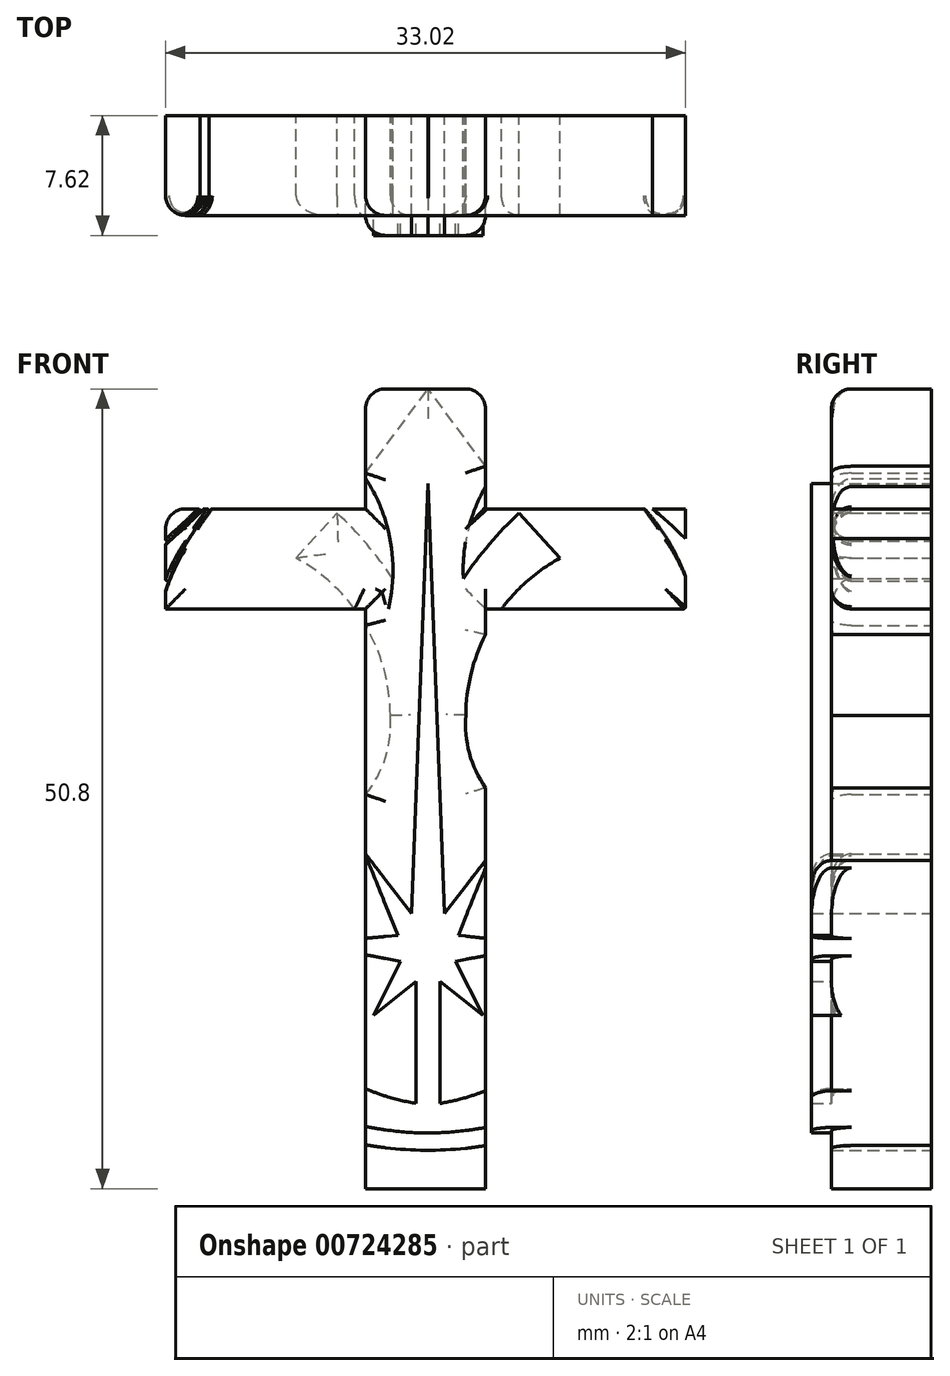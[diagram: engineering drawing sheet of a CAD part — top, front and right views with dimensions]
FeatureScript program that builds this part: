
annotation { "Feature Type Name" : "Feature", "Feature Type Description" : "" }
export const myFeature = defineFeature(function(context is Context, id is Id, definition is map)
    precondition{}
    {
        {
            var Q0;
            Q0=qCreatedBy(makeId("Front.planeOp"),FACE);
            var sketch = newSketch(context, id + "F0", { "sketchPlane" : qUnion([Q0])});
            skLineSegment(sketch, "E0", {"start": v(0, 50.8) * mm, "end": v(-7.62, 50.8) * mm});
            skLineSegment(sketch, "E1", {"start": v(-7.62, 0) * mm, "end": v(0, 0) * mm});
            skLineSegment(sketch, "E2", {"start": v(-7.62, 43.18) * mm, "end": v(-20.32, 43.18) * mm});
            skLineSegment(sketch, "E3", {"start": v(-20.32, 43.18) * mm, "end": v(-20.32, 36.83) * mm});
            skLineSegment(sketch, "E4", {"start": v(12.7, 36.83) * mm, "end": v(12.7, 43.18) * mm});
            skLineSegment(sketch, "E5", {"start": v(12.7, 43.18) * mm, "end": v(0, 43.18) * mm});
            skLineSegment(sketch, "E6", {"start": v(-20.32, 36.83) * mm, "end": v(-7.62, 36.83) * mm});
            skLineSegment(sketch, "E7", {"start": v(12.7, 36.83) * mm, "end": v(0, 36.83) * mm});
            skLineSegment(sketch, "E8", {"start": v(-7.62, 0) * mm, "end": v(-7.62, 36.83) * mm});
            skLineSegment(sketch, "E9", {"start": v(0, 36.83) * mm, "end": v(0, 0) * mm});
            skLineSegment(sketch, "E10", {"start": v(0, 43.18) * mm, "end": v(0, 50.8) * mm});
            skLineSegment(sketch, "E11", {"start": v(-7.62, 43.18) * mm, "end": v(-7.62, 50.8) * mm});
            skSolve(sketch);
        }
        {
            var Q0;
            Q0=qCreatedBy(makeId("Front.planeOp"),FACE);
            var sketch = newSketch(context, id + "F1", { "sketchPlane" : qUnion([Q0])});
            skArc(sketch, "E12", {"start": v(-17.9, 43.18) * mm, "mid": v(-19.15, 42.1) * mm, "end": v(-20.32, 40.94) * mm});
            skArc(sketch, "E13", {"start": v(-7.62, 3.95) * mm, "mid": v(-5.64, 3.65) * mm, "end": v(-3.65, 3.53) * mm});
            skArc(sketch, "E14", {"start": v(-7.62, 6.35) * mm, "mid": v(-6.04, 5.78) * mm, "end": v(-4.4, 5.41) * mm});
            skArc(sketch, "E15", {"start": v(-5.9, 38.75) * mm, "mid": v(-6.25, 42.07) * mm, "end": v(-7.62, 45.11) * mm});
            skArc(sketch, "E16", {"start": v(-5.9, 38.75) * mm, "mid": v(-7.54, 40.93) * mm, "end": v(-9.43, 42.9) * mm});
            skArc(sketch, "E17", {"start": v(-17.4, 43.18) * mm, "mid": v(-19.16, 40.71) * mm, "end": v(-20.32, 37.92) * mm});
            skArc(sketch, "E18", {"start": v(-7.62, 25.04) * mm, "mid": v(-6.35, 27.4) * mm, "end": v(-6.05, 30.07) * mm});
            skArc(sketch, "E19", {"start": v(-6.05, 30.07) * mm, "mid": v(-6.46, 33.03) * mm, "end": v(-7.62, 35.78) * mm});
            skLineSegment(sketch, "E20", {"start": v(-12.04, 40.06) * mm, "end": v(-9.43, 42.9) * mm});
            skLineSegment(sketch, "E21", {"start": v(-7.62, 45.45) * mm, "end": v(-3.65, 50.82) * mm});
            skLineSegment(sketch, "E22", {"start": v(-4.4, 5.41) * mm, "end": v(-4.4, 13.16) * mm});
            skLineSegment(sketch, "E23", {"start": v(-4.4, 13.16) * mm, "end": v(-7.12, 11) * mm});
            skLineSegment(sketch, "E24", {"start": v(-7.12, 11) * mm, "end": v(-5.4, 14.45) * mm});
            skLineSegment(sketch, "E25", {"start": v(-5.4, 14.45) * mm, "end": v(-7.62, 14.86) * mm});
            skLineSegment(sketch, "E26", {"start": v(-5.57, 16.1) * mm, "end": v(-7.62, 21.17) * mm});
            skLineSegment(sketch, "E27", {"start": v(-7.62, 21.26) * mm, "end": v(-4.7, 17.49) * mm});
            skLineSegment(sketch, "E28", {"start": v(-4.7, 17.49) * mm, "end": v(-3.65, 44.78) * mm});
            skLineSegment(sketch, "E29.MirrorCS", {"start": v(0, 45.88) * mm, "end": v(-3.65, 50.82) * mm});
            skArc(sketch, "E30.MirrorCS", {"start": v(-1.4, 38.75) * mm, "mid": v(0.24, 40.93) * mm, "end": v(2.13, 42.9) * mm});
            skLineSegment(sketch, "E31.MirrorCS", {"start": v(4.74, 40.06) * mm, "end": v(2.13, 42.9) * mm});
            skArc(sketch, "E32.MirrorCS", {"start": v(-1.25, 30.07) * mm, "mid": v(-0.92, 32.7) * mm, "end": v(0, 35.19) * mm});
            skArc(sketch, "E33.MirrorCS", {"start": v(0, 25.47) * mm, "mid": v(-1.02, 27.66) * mm, "end": v(-1.25, 30.07) * mm});
            skArc(sketch, "E34.MirrorCS", {"start": v(10.11, 43.18) * mm, "mid": v(11.6, 41.16) * mm, "end": v(12.7, 38.9) * mm});
            skArc(sketch, "E35.MirrorCS", {"start": v(0, 3.89) * mm, "mid": v(-1.82, 3.63) * mm, "end": v(-3.65, 3.53) * mm});
            skLineSegment(sketch, "E36.MirrorCS", {"start": v(-2.9, 5.41) * mm, "end": v(-2.9, 13.16) * mm});
            skLineSegment(sketch, "E37.MirrorCS", {"start": v(-2.9, 13.16) * mm, "end": v(-0.18, 11) * mm});
            skLineSegment(sketch, "E38.MirrorCS", {"start": v(-0.18, 11) * mm, "end": v(-1.9, 14.45) * mm});
            skLineSegment(sketch, "E39.MirrorCS", {"start": v(-1.9, 14.45) * mm, "end": v(0, 14.8) * mm});
            skLineSegment(sketch, "E40.MirrorCS", {"start": v(0, 15.9) * mm, "end": v(-1.73, 16.1) * mm});
            skLineSegment(sketch, "E41.MirrorCS", {"start": v(-1.73, 16.1) * mm, "end": v(0, 20.37) * mm});
            skLineSegment(sketch, "E42.MirrorCS", {"start": v(0, 20.85) * mm, "end": v(-2.6, 17.49) * mm});
            skLineSegment(sketch, "E43.MirrorCS", {"start": v(-2.6, 17.49) * mm, "end": v(-3.65, 44.78) * mm});
            skArc(sketch, "E44.MirrorCS", {"start": v(-1.4, 38.75) * mm, "mid": v(-1.12, 41.77) * mm, "end": v(0, 44.59) * mm});
            skArc(sketch, "E45.MirrorCS", {"start": v(0, 6.22) * mm, "mid": v(-1.43, 5.74) * mm, "end": v(-2.9, 5.41) * mm});
            skLineSegment(sketch, "E46.0.0", {"start": v(0, 0) * mm, "end": v(0, 36.83) * mm});
            skLineSegment(sketch, "E46.0.1", {"start": v(0, 36.83) * mm, "end": v(12.7, 36.83) * mm});
            skLineSegment(sketch, "E46.0.2", {"start": v(12.7, 36.83) * mm, "end": v(12.7, 43.18) * mm});
            skLineSegment(sketch, "E46.0.3", {"start": v(12.7, 43.18) * mm, "end": v(0, 43.18) * mm});
            skLineSegment(sketch, "E46.0.4", {"start": v(0, 43.18) * mm, "end": v(0, 50.8) * mm});
            skLineSegment(sketch, "E46.0.5", {"start": v(0, 50.8) * mm, "end": v(-7.62, 50.8) * mm});
            skLineSegment(sketch, "E46.0.6", {"start": v(-7.62, 50.8) * mm, "end": v(-7.62, 43.18) * mm});
            skLineSegment(sketch, "E46.0.7", {"start": v(-7.62, 43.18) * mm, "end": v(-20.32, 43.18) * mm});
            skLineSegment(sketch, "E46.0.8", {"start": v(-20.32, 43.18) * mm, "end": v(-20.32, 36.83) * mm});
            skLineSegment(sketch, "E46.0.9", {"start": v(-20.32, 36.83) * mm, "end": v(-7.62, 36.83) * mm});
            skLineSegment(sketch, "E46.0.10", {"start": v(-7.62, 36.83) * mm, "end": v(-7.62, 0) * mm});
            skLineSegment(sketch, "E46.0.11", {"start": v(-7.62, 0) * mm, "end": v(0, 0) * mm});
            skArc(sketch, "E47.trimOffspring", {"start": v(-7.62, 2.79) * mm, "mid": v(-3.81, 2.44) * mm, "end": v(0, 2.73) * mm});
            skArc(sketch, "E48.trimOffspring", {"start": v(12.7, 41.28) * mm, "mid": v(11.68, 42.26) * mm, "end": v(10.6, 43.18) * mm});
            skPoint(sketch, "E49.end.orphan", {"position": v(-18.43, 15.28) * mm});
            skPoint(sketch, "E50.end.orphan", {"position": v(-18.43, 11.36) * mm});
            skLineSegment(sketch, "E51", {"start": v(-5.57, 16.1) * mm, "end": v(-7.62, 15.9) * mm});
            skArc(sketch, "E52.trimOffspring", {"start": v(1.02, 36.83) * mm, "mid": v(2.7, 38.65) * mm, "end": v(4.74, 40.06) * mm});
            skArc(sketch, "E53.trimOffspring", {"start": v(-8.32, 36.83) * mm, "mid": v(-10, 38.65) * mm, "end": v(-12.04, 40.06) * mm});
            skSolve(sketch);
        }
        {
            var Q0;
            {var subQ4=sQuery(id+"F1.wireOp",EDGE,"E13");Q0=makeQuery(id+"F1.imprint","IMPRINT",FACE,{"disambiguationData":[TD([[makeQuery(id+"F1.imprint","IMPRINT",EDGE,{"derivedFrom":subQ4}),1.0]])]});}
            extrude(context, id + "F2", {"entities" : qUnion([Q0]), "depth" : 7.62 * mm, "offsetDistance" : 25.4 * mm});
        }
        {
            var Q0;
            {var subQ0=sQuery(id+"F1.wireOp",EDGE,"E12");Q0=makeQuery(id+"F1.imprint","IMPRINT",FACE,{"disambiguationData":[TD([[makeQuery(id+"F1.imprint","IMPRINT",EDGE,{"derivedFrom":subQ0}),1.0]])]});}
            var Q1;
            {var subQ0=sQuery(id+"F1.wireOp",EDGE,"E34.MirrorCS");Q1=makeQuery(id+"F1.imprint","IMPRINT",FACE,{"disambiguationData":[TD([[makeQuery(id+"F1.imprint","IMPRINT",EDGE,{"derivedFrom":subQ0}),1.0]])]});}
            var Q2;
            {var subQ1=sQuery(id+"F1.wireOp",EDGE,"E15");Q2=makeQuery(id+"F1.imprint","IMPRINT",FACE,{"disambiguationData":[TD([[makeQuery(id+"F1.imprint","IMPRINT",EDGE,{"derivedFrom":subQ1}),-1.0]])]});}
            var Q3;
            Q3=makeQuery(id+"F1.imprint","IMPRINT",FACE,{"disambiguationData":[TD([[makeQuery(id+"F1.imprint","IMPRINT",EDGE,{"derivedFrom":sQuery(id+"F1.wireOp",EDGE,"E36.MirrorCS")}),-1.0]])]});
            var Q4;
            {var subQ0=sQuery(id+"F1.wireOp",EDGE,"E40.MirrorCS");Q4=makeQuery(id+"F1.imprint","IMPRINT",FACE,{"disambiguationData":[TD([[makeQuery(id+"F1.imprint","IMPRINT",EDGE,{"derivedFrom":subQ0}),-1.0]])]});}
            var Q5;
            {var subQ0=sQuery(id+"F1.wireOp",EDGE,"E26");Q5=makeQuery(id+"F1.imprint","IMPRINT",FACE,{"disambiguationData":[TD([[makeQuery(id+"F1.imprint","IMPRINT",EDGE,{"derivedFrom":subQ0}),1.0]])]});}
            var Q6;
            {var subQ0=sQuery(id+"F1.wireOp",EDGE,"E14");Q6=makeQuery(id+"F1.imprint","IMPRINT",FACE,{"disambiguationData":[TD([[makeQuery(id+"F1.imprint","IMPRINT",EDGE,{"derivedFrom":subQ0}),1.0]])]});}
            var Q7;
            {var subQ1=sQuery(id+"F1.wireOp",EDGE,"E13");Q7=makeQuery(id+"F1.imprint","IMPRINT",FACE,{"disambiguationData":[TD([[makeQuery(id+"F1.imprint","IMPRINT",EDGE,{"derivedFrom":subQ1}),-1.0]])]});}
            extrude(context, id + "F3", {"entities" : qUnion([Q0, Q1, Q2, Q3, Q4, Q5, Q6, Q7]), "operationType" : NewBodyOperationType.ADD, "depth" : 6.35 * mm, "offsetDistance" : 25.4 * mm});
        }
        {
            var Q0;
            {var subQ3=sQuery(id+"F1.wireOp",EDGE,"E48.trimOffspring");Q0=makeQuery(id+"F1.imprint","IMPRINT",FACE,{"disambiguationData":[TD([[makeQuery(id+"F1.imprint","IMPRINT",EDGE,{"derivedFrom":subQ3}),-1.0]])]});}
            var Q1;
            Q1=makeQuery(id+"F1.imprint","IMPRINT",FACE,{"disambiguationData":[TD([[makeQuery(id+"F1.imprint","IMPRINT",EDGE,{"derivedFrom":sQuery(id+"F1.wireOp",EDGE,"E30.MirrorCS")}),1.0]])]});
            var Q2;
            {var subQ0=sQuery(id+"F1.wireOp",EDGE,"E46.0.4");var subQ1=sQuery(id+"F1.wireOp",EDGE,"E29.MirrorCS");var subQ2=makeQuery(id+"F1.imprint","INTERSECT",VERTEX,{"derivedFrom":[subQ1,subQ0]});Q2=makeQuery(id+"F1.imprint","IMPRINT",FACE,{"disambiguationData":[TD([[makeQuery(id+"F1.imprint","IMPRINT",EDGE,{"disambiguationData":[TD([[subQ2,-1.0]])],"derivedFrom":subQ1}),-1.0]])]});}
            var Q3;
            {var subQ0=sQuery(id+"F1.wireOp",EDGE,"E46.0.6");var subQ1=sQuery(id+"F1.wireOp",EDGE,"E21");var subQ2=makeQuery(id+"F1.imprint","INTERSECT",VERTEX,{"derivedFrom":[subQ1,subQ0]});Q3=makeQuery(id+"F1.imprint","IMPRINT",FACE,{"disambiguationData":[TD([[makeQuery(id+"F1.imprint","IMPRINT",EDGE,{"disambiguationData":[TD([[subQ2,-1.0]])],"derivedFrom":subQ1}),1.0]])]});}
            var Q4;
            {var subQ4=sQuery(id+"F1.wireOp",EDGE,"E15");Q4=makeQuery(id+"F1.imprint","IMPRINT",FACE,{"disambiguationData":[TD([[makeQuery(id+"F1.imprint","IMPRINT",EDGE,{"derivedFrom":subQ4}),1.0]])]});}
            var Q5;
            {var subQ0=sQuery(id+"F1.wireOp",EDGE,"E12");Q5=makeQuery(id+"F1.imprint","IMPRINT",FACE,{"disambiguationData":[TD([[makeQuery(id+"F1.imprint","IMPRINT",EDGE,{"derivedFrom":subQ0}),-1.0]])]});}
            var Q6;
            {var subQ0=sQuery(id+"F1.wireOp",EDGE,"E32.MirrorCS");Q6=makeQuery(id+"F1.imprint","IMPRINT",FACE,{"disambiguationData":[TD([[makeQuery(id+"F1.imprint","IMPRINT",EDGE,{"derivedFrom":subQ0}),-1.0]])]});}
            var Q7;
            {var subQ0=sQuery(id+"F1.wireOp",EDGE,"E18");Q7=makeQuery(id+"F1.imprint","IMPRINT",FACE,{"disambiguationData":[TD([[makeQuery(id+"F1.imprint","IMPRINT",EDGE,{"derivedFrom":subQ0}),1.0]])]});}
            var Q8;
            {var subQ0=sQuery(id+"F1.wireOp",EDGE,"E46.0.11");Q8=makeQuery(id+"F1.imprint","IMPRINT",FACE,{"disambiguationData":[TD([[makeQuery(id+"F1.imprint","IMPRINT",EDGE,{"derivedFrom":subQ0}),1.0]])]});}
            extrude(context, id + "F4", {"entities" : qUnion([Q0, Q1, Q2, Q3, Q4, Q5, Q6, Q7, Q8]), "depth" : 6.35 * mm, "offsetDistance" : 25.4 * mm});
        }
        {
            var Q0;
            {var subQ0=sQuery(id+"F1.wireOp",EDGE,"E46.0.7");Q0=makeQuery(id+"F4.opExtrude","CAP_EDGE",EDGE,{"disambiguationData":[OSD([subQ0]),TDD([makeQuery(id+"F1.imprint","IMPRINT",EDGE,{"disambiguationData":[TD([[makeQuery(id+"F1.imprint","INTERSECT",VERTEX,{"derivedFrom":[sQuery(id+"F1.wireOp",EDGE,"E17"),subQ0]}),1.0]])],"derivedFrom":subQ0})])],"isStart":false});}
            var Q1;
            Q1=makeQuery(id+"F3.opExtrude","CAP_EDGE",EDGE,{"disambiguationData":[OSD([sQuery(id+"F1.wireOp",EDGE,"E46.0.7")])],"isStart":false});
            var Q2;
            {var subQ0=sQuery(id+"F1.wireOp",EDGE,"E46.0.7");Q2=makeQuery(id+"F4.opExtrude","CAP_EDGE",EDGE,{"disambiguationData":[OSD([subQ0]),TDD([makeQuery(id+"F1.imprint","IMPRINT",EDGE,{"disambiguationData":[TD([[makeQuery(id+"F1.imprint","INTERSECT",VERTEX,{"derivedFrom":[sQuery(id+"F1.wireOp",EDGE,"E12"),subQ0]}),-1.0]])],"derivedFrom":subQ0})])],"isStart":false});}
            var Q3;
            {var subQ0=sQuery(id+"F1.wireOp",EDGE,"E46.0.5");Q3=makeQuery(id+"F4.opExtrude","CAP_EDGE",EDGE,{"disambiguationData":[OSD([subQ0]),TDD([makeQuery(id+"F1.imprint","IMPRINT",EDGE,{"disambiguationData":[TD([[makeQuery(id+"F1.imprint","INTERSECT",VERTEX,{"derivedFrom":[sQuery(id+"F1.wireOp",EDGE,"E46.0.4"),subQ0]}),-1.0]])],"derivedFrom":subQ0})])],"isStart":false});}
            var Q4;
            {var subQ0=sQuery(id+"F1.wireOp",EDGE,"E46.0.5");Q4=makeQuery(id+"F4.opExtrude","CAP_EDGE",EDGE,{"disambiguationData":[OSD([subQ0]),TDD([makeQuery(id+"F1.imprint","IMPRINT",EDGE,{"disambiguationData":[TD([[makeQuery(id+"F1.imprint","INTERSECT",VERTEX,{"derivedFrom":[subQ0,sQuery(id+"F1.wireOp",EDGE,"E46.0.6")]}),1.0]])],"derivedFrom":subQ0})])],"isStart":false});}
            var Q5;
            Q5=makeQuery(id+"F3.opExtrude","CAP_EDGE",EDGE,{"disambiguationData":[OSD([sQuery(id+"F1.wireOp",EDGE,"E29.MirrorCS")])],"isStart":false});
            var Q6;
            Q6=makeQuery(id+"F3.opExtrude","CAP_EDGE",EDGE,{"disambiguationData":[OSD([sQuery(id+"F1.wireOp",EDGE,"E21")])],"isStart":false});
            var Q7;
            Q7=makeQuery(id+"F4.opExtrude","SWEPT_EDGE",EDGE,{"disambiguationData":[OSD([sQuery(id+"F1.wireOp",EDGE,"E46.0.4"),sQuery(id+"F1.wireOp",EDGE,"E46.0.5")])]});
            var Q8;
            Q8=makeQuery(id+"F4.opExtrude","SWEPT_EDGE",EDGE,{"disambiguationData":[OSD([sQuery(id+"F1.wireOp",EDGE,"E46.0.5"),sQuery(id+"F1.wireOp",EDGE,"E46.0.6")])]});
            var Q9;
            Q9=makeQuery(id+"F4.opExtrude","CAP_EDGE",EDGE,{"disambiguationData":[OSD([sQuery(id+"F1.wireOp",EDGE,"E46.0.9")])],"isStart":false});
            var Q10;
            {var subQ0=sQuery(id+"F1.wireOp",EDGE,"E46.0.4");Q10=makeQuery(id+"F4.opExtrude","CAP_EDGE",EDGE,{"disambiguationData":[OSD([subQ0]),TDD([makeQuery(id+"F1.imprint","IMPRINT",EDGE,{"disambiguationData":[TD([[makeQuery(id+"F1.imprint","INTERSECT",VERTEX,{"derivedFrom":[sQuery(id+"F1.wireOp",EDGE,"E29.MirrorCS"),subQ0]}),-1.0]])],"derivedFrom":subQ0})])],"isStart":false});}
            var Q11;
            Q11=makeQuery(id+"F3.opExtrude","CAP_EDGE",EDGE,{"disambiguationData":[OSD([sQuery(id+"F1.wireOp",EDGE,"E46.0.4")])],"isStart":false});
            var Q12;
            {var subQ0=sQuery(id+"F1.wireOp",EDGE,"E46.0.6");Q12=makeQuery(id+"F4.opExtrude","CAP_EDGE",EDGE,{"disambiguationData":[OSD([subQ0]),TDD([makeQuery(id+"F1.imprint","IMPRINT",EDGE,{"disambiguationData":[TD([[makeQuery(id+"F1.imprint","INTERSECT",VERTEX,{"derivedFrom":[sQuery(id+"F1.wireOp",EDGE,"E21"),subQ0]}),1.0]])],"derivedFrom":subQ0})])],"isStart":false});}
            var Q13;
            Q13=makeQuery(id+"F3.opExtrude","CAP_EDGE",EDGE,{"disambiguationData":[OSD([sQuery(id+"F1.wireOp",EDGE,"E46.0.6")])],"isStart":false});
            var Q14;
            {var subQ0=sQuery(id+"F1.wireOp",EDGE,"E46.0.6");Q14=makeQuery(id+"F4.opExtrude","CAP_EDGE",EDGE,{"disambiguationData":[OSD([subQ0]),TDD([makeQuery(id+"F1.imprint","IMPRINT",EDGE,{"disambiguationData":[TD([[makeQuery(id+"F1.imprint","INTERSECT",VERTEX,{"derivedFrom":[sQuery(id+"F1.wireOp",EDGE,"E15"),subQ0]}),-1.0]])],"derivedFrom":subQ0})])],"isStart":false});}
            var Q15;
            {var subQ0=sQuery(id+"F1.wireOp",EDGE,"E46.0.3");Q15=makeQuery(id+"F4.opExtrude","CAP_EDGE",EDGE,{"disambiguationData":[OSD([subQ0]),TDD([makeQuery(id+"F1.imprint","IMPRINT",EDGE,{"disambiguationData":[TD([[makeQuery(id+"F1.imprint","INTERSECT",VERTEX,{"derivedFrom":[sQuery(id+"F1.wireOp",EDGE,"E34.MirrorCS"),subQ0]}),-1.0]])],"derivedFrom":subQ0})])],"isStart":false});}
            var Q16;
            Q16=makeQuery(id+"F3.opExtrude","CAP_EDGE",EDGE,{"disambiguationData":[OSD([sQuery(id+"F1.wireOp",EDGE,"E46.0.3")])],"isStart":false});
            var Q17;
            {var subQ0=sQuery(id+"F1.wireOp",EDGE,"E46.0.3");Q17=makeQuery(id+"F4.opExtrude","CAP_EDGE",EDGE,{"disambiguationData":[OSD([subQ0]),TDD([makeQuery(id+"F1.imprint","IMPRINT",EDGE,{"disambiguationData":[TD([[makeQuery(id+"F1.imprint","INTERSECT",VERTEX,{"derivedFrom":[sQuery(id+"F1.wireOp",EDGE,"E46.0.2"),subQ0]}),-1.0]])],"derivedFrom":subQ0})])],"isStart":false});}
            var Q18;
            {var subQ0=sQuery(id+"F1.wireOp",EDGE,"E46.0.2");Q18=makeQuery(id+"F4.opExtrude","CAP_EDGE",EDGE,{"disambiguationData":[OSD([subQ0]),TDD([makeQuery(id+"F1.imprint","IMPRINT",EDGE,{"disambiguationData":[TD([[makeQuery(id+"F1.imprint","INTERSECT",VERTEX,{"derivedFrom":[sQuery(id+"F1.wireOp",EDGE,"E34.MirrorCS"),subQ0]}),1.0]])],"derivedFrom":subQ0})])],"isStart":false});}
            var Q19;
            Q19=makeQuery(id+"F3.opExtrude","CAP_EDGE",EDGE,{"disambiguationData":[OSD([sQuery(id+"F1.wireOp",EDGE,"E46.0.2")])],"isStart":false});
            var Q20;
            {var subQ0=sQuery(id+"F1.wireOp",EDGE,"E46.0.8");Q20=makeQuery(id+"F4.opExtrude","CAP_EDGE",EDGE,{"disambiguationData":[OSD([subQ0]),TDD([makeQuery(id+"F1.imprint","IMPRINT",EDGE,{"disambiguationData":[TD([[makeQuery(id+"F1.imprint","INTERSECT",VERTEX,{"derivedFrom":[sQuery(id+"F1.wireOp",EDGE,"E17"),subQ0]}),-1.0]])],"derivedFrom":subQ0})])],"isStart":false});}
            var Q21;
            Q21=makeQuery(id+"F3.opExtrude","CAP_EDGE",EDGE,{"disambiguationData":[OSD([sQuery(id+"F1.wireOp",EDGE,"E46.0.8")])],"isStart":false});
            var Q22;
            Q22=makeQuery(id+"F3.opExtrude","CAP_EDGE",EDGE,{"disambiguationData":[OSD([sQuery(id+"F1.wireOp",EDGE,"E46.0.1")])],"isStart":false});
            var Q23;
            {var subQ0=sQuery(id+"F1.wireOp",EDGE,"E46.0.0");Q23=makeQuery(id+"F3.opExtrude","CAP_EDGE",EDGE,{"disambiguationData":[OSD([subQ0]),TDD([makeQuery(id+"F1.imprint","IMPRINT",EDGE,{"disambiguationData":[TD([[makeQuery(id+"F1.imprint","INTERSECT",VERTEX,{"derivedFrom":[sQuery(id+"F1.wireOp",EDGE,"E32.MirrorCS"),subQ0]}),-1.0]])],"derivedFrom":subQ0})])],"isStart":false});}
            var Q24;
            {var subQ0=sQuery(id+"F1.wireOp",EDGE,"E46.0.0");Q24=makeQuery(id+"F4.opExtrude","CAP_EDGE",EDGE,{"disambiguationData":[OSD([subQ0]),TDD([makeQuery(id+"F1.imprint","IMPRINT",EDGE,{"disambiguationData":[TD([[makeQuery(id+"F1.imprint","INTERSECT",VERTEX,{"derivedFrom":[sQuery(id+"F1.wireOp",EDGE,"E32.MirrorCS"),subQ0]}),1.0]])],"derivedFrom":subQ0})])],"isStart":false});}
            var Q25;
            {var subQ0=sQuery(id+"F1.wireOp",EDGE,"E46.0.0");Q25=makeQuery(id+"F3.opExtrude","CAP_EDGE",EDGE,{"disambiguationData":[OSD([subQ0]),TDD([makeQuery(id+"F1.imprint","IMPRINT",EDGE,{"disambiguationData":[TD([[makeQuery(id+"F1.imprint","INTERSECT",VERTEX,{"derivedFrom":[sQuery(id+"F1.wireOp",EDGE,"E33.MirrorCS"),subQ0]}),1.0]])],"derivedFrom":subQ0})])],"isStart":false});}
            var Q26;
            {var subQ0=sQuery(id+"F1.wireOp",EDGE,"E46.0.0");Q26=makeQuery(id+"F2.opExtrude","CAP_EDGE",EDGE,{"disambiguationData":[OSD([subQ0]),TDD([makeQuery(id+"F1.imprint","IMPRINT",EDGE,{"disambiguationData":[TD([[makeQuery(id+"F1.imprint","INTERSECT",VERTEX,{"derivedFrom":[sQuery(id+"F1.wireOp",EDGE,"E41.MirrorCS"),subQ0]}),-1.0]])],"derivedFrom":subQ0})])],"isStart":false});}
            var Q27;
            {var subQ0=sQuery(id+"F1.wireOp",EDGE,"E46.0.0");Q27=makeQuery(id+"F3.opExtrude","CAP_EDGE",EDGE,{"disambiguationData":[OSD([subQ0]),TDD([makeQuery(id+"F1.imprint","IMPRINT",EDGE,{"disambiguationData":[TD([[makeQuery(id+"F1.imprint","INTERSECT",VERTEX,{"derivedFrom":[sQuery(id+"F1.wireOp",EDGE,"E40.MirrorCS"),subQ0]}),-1.0]])],"derivedFrom":subQ0})])],"isStart":false});}
            var Q28;
            {var subQ0=sQuery(id+"F1.wireOp",EDGE,"E46.0.0");Q28=makeQuery(id+"F2.opExtrude","CAP_EDGE",EDGE,{"disambiguationData":[OSD([subQ0]),TDD([makeQuery(id+"F1.imprint","IMPRINT",EDGE,{"disambiguationData":[TD([[makeQuery(id+"F1.imprint","INTERSECT",VERTEX,{"derivedFrom":[sQuery(id+"F1.wireOp",EDGE,"E39.MirrorCS"),subQ0]}),-1.0]])],"derivedFrom":subQ0})])],"isStart":false});}
            var Q29;
            {var subQ0=sQuery(id+"F1.wireOp",EDGE,"E46.0.0");Q29=makeQuery(id+"F3.opExtrude","CAP_EDGE",EDGE,{"disambiguationData":[OSD([subQ0]),TDD([makeQuery(id+"F1.imprint","IMPRINT",EDGE,{"disambiguationData":[TD([[makeQuery(id+"F1.imprint","INTERSECT",VERTEX,{"derivedFrom":[sQuery(id+"F1.wireOp",EDGE,"E39.MirrorCS"),subQ0]}),1.0]])],"derivedFrom":subQ0})])],"isStart":false});}
            var Q30;
            {var subQ0=sQuery(id+"F1.wireOp",EDGE,"E46.0.0");Q30=makeQuery(id+"F2.opExtrude","CAP_EDGE",EDGE,{"disambiguationData":[OSD([subQ0]),TDD([makeQuery(id+"F1.imprint","IMPRINT",EDGE,{"disambiguationData":[TD([[makeQuery(id+"F1.imprint","INTERSECT",VERTEX,{"derivedFrom":[sQuery(id+"F1.wireOp",EDGE,"E35.MirrorCS"),subQ0]}),-1.0]])],"derivedFrom":subQ0})])],"isStart":false});}
            var Q31;
            {var subQ0=sQuery(id+"F1.wireOp",EDGE,"E46.0.0");Q31=makeQuery(id+"F3.opExtrude","CAP_EDGE",EDGE,{"disambiguationData":[OSD([subQ0]),TDD([makeQuery(id+"F1.imprint","IMPRINT",EDGE,{"disambiguationData":[TD([[makeQuery(id+"F1.imprint","INTERSECT",VERTEX,{"derivedFrom":[sQuery(id+"F1.wireOp",EDGE,"E35.MirrorCS"),subQ0]}),1.0]])],"derivedFrom":subQ0})])],"isStart":false});}
            var Q32;
            {var subQ0=sQuery(id+"F1.wireOp",EDGE,"E46.0.0");Q32=makeQuery(id+"F4.opExtrude","CAP_EDGE",EDGE,{"disambiguationData":[OSD([subQ0]),TDD([makeQuery(id+"F1.imprint","IMPRINT",EDGE,{"disambiguationData":[TD([[makeQuery(id+"F1.imprint","INTERSECT",VERTEX,{"derivedFrom":[subQ0,sQuery(id+"F1.wireOp",EDGE,"E46.0.11")]}),-1.0]])],"derivedFrom":subQ0})])],"isStart":false});}
            var Q33;
            {var subQ0=sQuery(id+"F1.wireOp",EDGE,"E46.0.10");Q33=makeQuery(id+"F4.opExtrude","CAP_EDGE",EDGE,{"disambiguationData":[OSD([subQ0]),TDD([makeQuery(id+"F1.imprint","IMPRINT",EDGE,{"disambiguationData":[TD([[makeQuery(id+"F1.imprint","INTERSECT",VERTEX,{"derivedFrom":[subQ0,sQuery(id+"F1.wireOp",EDGE,"E46.0.11")]}),1.0]])],"derivedFrom":subQ0})])],"isStart":false});}
            var Q34;
            {var subQ0=sQuery(id+"F1.wireOp",EDGE,"E46.0.10");Q34=makeQuery(id+"F2.opExtrude","CAP_EDGE",EDGE,{"disambiguationData":[OSD([subQ0]),TDD([makeQuery(id+"F1.imprint","IMPRINT",EDGE,{"disambiguationData":[TD([[makeQuery(id+"F1.imprint","INTERSECT",VERTEX,{"derivedFrom":[sQuery(id+"F1.wireOp",EDGE,"E13"),subQ0]}),1.0]])],"derivedFrom":subQ0})])],"isStart":false});}
            var Q35;
            {var subQ0=sQuery(id+"F1.wireOp",EDGE,"E46.0.10");Q35=makeQuery(id+"F3.opExtrude","CAP_EDGE",EDGE,{"disambiguationData":[OSD([subQ0]),TDD([makeQuery(id+"F1.imprint","IMPRINT",EDGE,{"disambiguationData":[TD([[makeQuery(id+"F1.imprint","INTERSECT",VERTEX,{"derivedFrom":[sQuery(id+"F1.wireOp",EDGE,"E13"),subQ0]}),-1.0]])],"derivedFrom":subQ0})])],"isStart":false});}
            var Q36;
            {var subQ0=sQuery(id+"F1.wireOp",EDGE,"E46.0.10");Q36=makeQuery(id+"F3.opExtrude","CAP_EDGE",EDGE,{"disambiguationData":[OSD([subQ0]),TDD([makeQuery(id+"F1.imprint","IMPRINT",EDGE,{"disambiguationData":[TD([[makeQuery(id+"F1.imprint","INTERSECT",VERTEX,{"derivedFrom":[sQuery(id+"F1.wireOp",EDGE,"E14"),subQ0]}),1.0]])],"derivedFrom":subQ0})])],"isStart":false});}
            var Q37;
            {var subQ0=sQuery(id+"F1.wireOp",EDGE,"E46.0.10");Q37=makeQuery(id+"F2.opExtrude","CAP_EDGE",EDGE,{"disambiguationData":[OSD([subQ0]),TDD([makeQuery(id+"F1.imprint","IMPRINT",EDGE,{"disambiguationData":[TD([[makeQuery(id+"F1.imprint","INTERSECT",VERTEX,{"derivedFrom":[sQuery(id+"F1.wireOp",EDGE,"E25"),subQ0]}),1.0]])],"derivedFrom":subQ0})])],"isStart":false});}
            var Q38;
            {var subQ0=sQuery(id+"F1.wireOp",EDGE,"E46.0.10");Q38=makeQuery(id+"F3.opExtrude","CAP_EDGE",EDGE,{"disambiguationData":[OSD([subQ0]),TDD([makeQuery(id+"F1.imprint","IMPRINT",EDGE,{"disambiguationData":[TD([[makeQuery(id+"F1.imprint","INTERSECT",VERTEX,{"derivedFrom":[sQuery(id+"F1.wireOp",EDGE,"E26"),subQ0]}),-1.0]])],"derivedFrom":subQ0})])],"isStart":false});}
            var Q39;
            {var subQ0=sQuery(id+"F1.wireOp",EDGE,"E46.0.10");Q39=makeQuery(id+"F2.opExtrude","CAP_EDGE",EDGE,{"disambiguationData":[OSD([subQ0]),TDD([makeQuery(id+"F1.imprint","IMPRINT",EDGE,{"disambiguationData":[TD([[makeQuery(id+"F1.imprint","INTERSECT",VERTEX,{"derivedFrom":[sQuery(id+"F1.wireOp",EDGE,"E26"),subQ0]}),1.0]])],"derivedFrom":subQ0})])],"isStart":false});}
            var Q40;
            {var subQ0=sQuery(id+"F1.wireOp",EDGE,"E46.0.10");Q40=makeQuery(id+"F3.opExtrude","CAP_EDGE",EDGE,{"disambiguationData":[OSD([subQ0]),TDD([makeQuery(id+"F1.imprint","IMPRINT",EDGE,{"disambiguationData":[TD([[makeQuery(id+"F1.imprint","INTERSECT",VERTEX,{"derivedFrom":[sQuery(id+"F1.wireOp",EDGE,"E18"),subQ0]}),-1.0]])],"derivedFrom":subQ0})])],"isStart":false});}
            var Q41;
            {var subQ0=sQuery(id+"F1.wireOp",EDGE,"E46.0.10");Q41=makeQuery(id+"F4.opExtrude","CAP_EDGE",EDGE,{"disambiguationData":[OSD([subQ0]),TDD([makeQuery(id+"F1.imprint","IMPRINT",EDGE,{"disambiguationData":[TD([[makeQuery(id+"F1.imprint","INTERSECT",VERTEX,{"derivedFrom":[sQuery(id+"F1.wireOp",EDGE,"E18"),subQ0]}),1.0]])],"derivedFrom":subQ0})])],"isStart":false});}
            var Q42;
            {var subQ0=sQuery(id+"F1.wireOp",EDGE,"E46.0.10");Q42=makeQuery(id+"F3.opExtrude","CAP_EDGE",EDGE,{"disambiguationData":[OSD([subQ0]),TDD([makeQuery(id+"F1.imprint","IMPRINT",EDGE,{"disambiguationData":[TD([[makeQuery(id+"F1.imprint","INTERSECT",VERTEX,{"derivedFrom":[sQuery(id+"F1.wireOp",EDGE,"E19"),subQ0]}),1.0]])],"derivedFrom":subQ0})])],"isStart":false});}
            var Q43;
            Q43=makeQuery(id+"F4.opExtrude","CAP_EDGE",EDGE,{"disambiguationData":[OSD([sQuery(id+"F1.wireOp",EDGE,"E46.0.1")])],"isStart":false});
            var Q44;
            Q44=makeQuery(id+"F3.opExtrude","CAP_EDGE",EDGE,{"disambiguationData":[OSD([sQuery(id+"F1.wireOp",EDGE,"E46.0.9")])],"isStart":false});
            var Q45;
            Q45=makeQuery(id+"F3.opExtrude","CAP_EDGE",EDGE,{"disambiguationData":[OSD([sQuery(id+"F1.wireOp",EDGE,"E31.MirrorCS")])],"isStart":false});
            var Q46;
            Q46=makeQuery(id+"F3.opExtrude","CAP_EDGE",EDGE,{"disambiguationData":[OSD([sQuery(id+"F1.wireOp",EDGE,"E30.MirrorCS")])],"isStart":false});
            var Q47;
            Q47=makeQuery(id+"F3.opExtrude","CAP_EDGE",EDGE,{"disambiguationData":[OSD([sQuery(id+"F1.wireOp",EDGE,"E32.MirrorCS")])],"isStart":false});
            var Q48;
            Q48=makeQuery(id+"F3.opExtrude","CAP_EDGE",EDGE,{"disambiguationData":[OSD([sQuery(id+"F1.wireOp",EDGE,"E19")])],"isStart":false});
            var Q49;
            Q49=makeQuery(id+"F3.opExtrude","CAP_EDGE",EDGE,{"disambiguationData":[OSD([sQuery(id+"F1.wireOp",EDGE,"E53.trimOffspring")])],"isStart":false});
            var Q50;
            Q50=makeQuery(id+"F3.opExtrude","CAP_EDGE",EDGE,{"disambiguationData":[OSD([sQuery(id+"F1.wireOp",EDGE,"E20")])],"isStart":false});
            var Q51;
            Q51=makeQuery(id+"F3.opExtrude","CAP_EDGE",EDGE,{"disambiguationData":[OSD([sQuery(id+"F1.wireOp",EDGE,"E16")])],"isStart":false});
            var Q52;
            Q52=makeQuery(id+"F3.opExtrude","CAP_EDGE",EDGE,{"disambiguationData":[OSD([sQuery(id+"F1.wireOp",EDGE,"E52.trimOffspring")])],"isStart":false});
            var Q53;
            Q53=makeQuery(id+"F3.opExtrude","CAP_EDGE",EDGE,{"disambiguationData":[OSD([sQuery(id+"F1.wireOp",EDGE,"E18")])],"isStart":false});
            var Q54;
            Q54=makeQuery(id+"F3.opExtrude","CAP_EDGE",EDGE,{"disambiguationData":[OSD([sQuery(id+"F1.wireOp",EDGE,"E33.MirrorCS")])],"isStart":false});
            fillet(context, id + "F5", {"entities" : qUnion([Q0, Q1, Q2, Q3, Q4, Q5, Q6, Q7, Q8, Q9, Q10, Q11, Q12, Q13, Q14, Q15, Q16, Q17, Q18, Q19, Q20, Q21, Q22, Q23, Q24, Q25, Q26, Q27, Q28, Q29, Q30, Q31, Q32, Q33, Q34, Q35, Q36, Q37, Q38, Q39, Q40, Q41, Q42, Q43, Q44, Q45, Q46, Q47, Q48, Q49, Q50, Q51, Q52, Q53, Q54]), "radius" : 1.27 * mm, "tangentPropagation" : true, "allowEdgeOverflow" : false});
        }
        {
            var Q0;
            {var subQ0=sQuery(id+"F1.wireOp",EDGE,"E46.0.3");var subQ1=sQuery(id+"F1.wireOp",EDGE,"E46.0.2");var subQ2=makeQuery(id+"F1.imprint","INTERSECT",VERTEX,{"derivedFrom":[subQ1,subQ0]});Q0=makeQuery(id+"F5.opFillet","BLEND_EDGE",EDGE,{"blendedFrom":[makeQuery(id+"F4.opExtrude","CAP_EDGE",EDGE,{"disambiguationData":[OSD([subQ0]),TDD([makeQuery(id+"F1.imprint","IMPRINT",EDGE,{"disambiguationData":[TD([[subQ2,-1.0]])],"derivedFrom":subQ0})])],"isStart":false}),makeQuery(id+"F4.opExtrude","SWEPT_FACE",FACE,{"disambiguationData":[OSD([subQ1]),TDD([makeQuery(id+"F1.imprint","IMPRINT",EDGE,{"disambiguationData":[TD([[subQ2,1.0]])],"derivedFrom":subQ1})])]})],"blendedInto":[makeQuery(id+"F4.opExtrude","SWEPT_FACE",FACE,{"disambiguationData":[OSD([subQ1]),TDD([makeQuery(id+"F1.imprint","IMPRINT",EDGE,{"disambiguationData":[TD([[subQ2,1.0]])],"derivedFrom":subQ1})])]})]});}
            var Q1;
            {var subQ0=sQuery(id+"F1.wireOp",EDGE,"E46.0.8");var subQ1=sQuery(id+"F1.wireOp",EDGE,"E12");var subQ2=sQuery(id+"F1.wireOp",EDGE,"E46.0.7");Q1=makeQuery(id+"F5.opFillet","BLEND_EDGE",EDGE,{"blendedFrom":[makeQuery(id+"F4.opExtrude","CAP_EDGE",EDGE,{"disambiguationData":[OSD([subQ2]),TDD([makeQuery(id+"F1.imprint","IMPRINT",EDGE,{"disambiguationData":[TD([[makeQuery(id+"F1.imprint","INTERSECT",VERTEX,{"derivedFrom":[subQ1,subQ2]}),-1.0]])],"derivedFrom":subQ2})])],"isStart":false}),makeQuery(id+"F4.opExtrude","SWEPT_FACE",FACE,{"disambiguationData":[OSD([subQ0]),TDD([makeQuery(id+"F1.imprint","IMPRINT",EDGE,{"disambiguationData":[TD([[makeQuery(id+"F1.imprint","INTERSECT",VERTEX,{"derivedFrom":[subQ1,subQ0]}),1.0]])],"derivedFrom":subQ0})])]})],"blendedInto":[makeQuery(id+"F4.opExtrude","SWEPT_FACE",FACE,{"disambiguationData":[OSD([subQ0]),TDD([makeQuery(id+"F1.imprint","IMPRINT",EDGE,{"disambiguationData":[TD([[makeQuery(id+"F1.imprint","INTERSECT",VERTEX,{"derivedFrom":[subQ1,subQ0]}),1.0]])],"derivedFrom":subQ0})])]})]});}
            fillet(context, id + "F6", {"entities" : qUnion([Q0, Q1]), "radius" : 1.27 * mm, "tangentPropagation" : true, "allowEdgeOverflow" : false});
        }
        {
            var Q0;
            Q0=makeQuery(id+"F3.opExtrude","SWEPT_EDGE",EDGE,{"disambiguationData":[OSD([sQuery(id+"F1.wireOp",EDGE,"E17"),sQuery(id+"F1.wireOp",EDGE,"E46.0.8")])]});
            var Q1;
            Q1=makeQuery(id+"F3.opExtrude","SWEPT_EDGE",EDGE,{"disambiguationData":[OSD([sQuery(id+"F1.wireOp",EDGE,"E12"),sQuery(id+"F1.wireOp",EDGE,"E46.0.8")])]});
            var Q2;
            {var subQ0=sQuery(id+"F1.wireOp",EDGE,"E17");var subQ1=sQuery(id+"F1.wireOp",EDGE,"E46.0.8");Q2=makeQuery(id+"F5.opFillet","BLEND_EDGE",EDGE,{"blendedFrom":[makeQuery(id+"F4.opExtrude","CAP_EDGE",EDGE,{"disambiguationData":[OSD([subQ1]),TDD([makeQuery(id+"F1.imprint","IMPRINT",EDGE,{"disambiguationData":[TD([[makeQuery(id+"F1.imprint","INTERSECT",VERTEX,{"derivedFrom":[subQ0,subQ1]}),-1.0]])],"derivedFrom":subQ1})])],"isStart":false}),makeQuery(id+"F4.opExtrude","SWEPT_FACE",FACE,{"disambiguationData":[OSD([subQ0])]})],"blendedInto":[makeQuery(id+"F4.opExtrude","SWEPT_FACE",FACE,{"disambiguationData":[OSD([subQ0])]})]});}
            var Q3;
            {var subQ0=sQuery(id+"F1.wireOp",EDGE,"E12");var subQ1=sQuery(id+"F1.wireOp",EDGE,"E46.0.8");Q3=makeQuery(id+"F6.opFillet","BLEND_EDGE",EDGE,{"blendedFrom":[makeQuery(id+"F4.opExtrude","CAP_EDGE",EDGE,{"disambiguationData":[OSD([subQ1]),TDD([makeQuery(id+"F1.imprint","IMPRINT",EDGE,{"disambiguationData":[TD([[makeQuery(id+"F1.imprint","INTERSECT",VERTEX,{"derivedFrom":[subQ0,subQ1]}),1.0]])],"derivedFrom":subQ1})])],"isStart":false}),makeQuery(id+"F4.opExtrude","SWEPT_FACE",FACE,{"disambiguationData":[OSD([subQ0])]})],"blendedInto":[makeQuery(id+"F4.opExtrude","SWEPT_FACE",FACE,{"disambiguationData":[OSD([subQ0])]})]});}
            var Q4;
            Q4=makeQuery(id+"F3.opExtrude","CAP_EDGE",EDGE,{"disambiguationData":[OSD([sQuery(id+"F1.wireOp",EDGE,"E17")])],"isStart":false});
            var Q5;
            Q5=makeQuery(id+"F5.opFillet","BLEND_EDGE",EDGE,{"blendedFrom":[makeQuery(id+"F3.opExtrude","CAP_EDGE",EDGE,{"disambiguationData":[OSD([sQuery(id+"F1.wireOp",EDGE,"E46.0.8")])],"isStart":false}),makeQuery(id+"F3.opExtrude","SWEPT_FACE",FACE,{"disambiguationData":[OSD([sQuery(id+"F1.wireOp",EDGE,"E12")])]})],"blendedInto":[makeQuery(id+"F3.opExtrude","SWEPT_FACE",FACE,{"disambiguationData":[OSD([sQuery(id+"F1.wireOp",EDGE,"E12")])]})]});
            var Q6;
            Q6=makeQuery(id+"F5.opFillet","BLEND_EDGE",EDGE,{"blendedFrom":[makeQuery(id+"F3.opExtrude","CAP_EDGE",EDGE,{"disambiguationData":[OSD([sQuery(id+"F1.wireOp",EDGE,"E46.0.7")])],"isStart":false}),makeQuery(id+"F3.opExtrude","SWEPT_FACE",FACE,{"disambiguationData":[OSD([sQuery(id+"F1.wireOp",EDGE,"E12")])]})],"blendedInto":[makeQuery(id+"F3.opExtrude","SWEPT_FACE",FACE,{"disambiguationData":[OSD([sQuery(id+"F1.wireOp",EDGE,"E12")])]})]});
            var Q7;
            Q7=makeQuery(id+"F5.opFillet","BLEND_EDGE",EDGE,{"blendedFrom":[makeQuery(id+"F3.opExtrude","CAP_EDGE",EDGE,{"disambiguationData":[OSD([sQuery(id+"F1.wireOp",EDGE,"E46.0.7")])],"isStart":false}),makeQuery(id+"F3.opExtrude","SWEPT_FACE",FACE,{"disambiguationData":[OSD([sQuery(id+"F1.wireOp",EDGE,"E17")])]})],"blendedInto":[makeQuery(id+"F3.opExtrude","SWEPT_FACE",FACE,{"disambiguationData":[OSD([sQuery(id+"F1.wireOp",EDGE,"E17")])]})]});
            var Q8;
            Q8=makeQuery(id+"F3.opExtrude","SWEPT_EDGE",EDGE,{"disambiguationData":[OSD([sQuery(id+"F1.wireOp",EDGE,"E12"),sQuery(id+"F1.wireOp",EDGE,"E46.0.7")])]});
            var Q9;
            Q9=makeQuery(id+"F3.opExtrude","SWEPT_EDGE",EDGE,{"disambiguationData":[OSD([sQuery(id+"F1.wireOp",EDGE,"E17"),sQuery(id+"F1.wireOp",EDGE,"E46.0.7")])]});
            var Q10;
            {var subQ0=sQuery(id+"F1.wireOp",EDGE,"E48.trimOffspring");var subQ1=sQuery(id+"F1.wireOp",EDGE,"E46.0.2");Q10=makeQuery(id+"F6.opFillet","BLEND_EDGE",EDGE,{"blendedFrom":[makeQuery(id+"F4.opExtrude","CAP_EDGE",EDGE,{"disambiguationData":[OSD([subQ1]),TDD([makeQuery(id+"F1.imprint","IMPRINT",EDGE,{"disambiguationData":[TD([[makeQuery(id+"F1.imprint","INTERSECT",VERTEX,{"derivedFrom":[subQ1,sQuery(id+"F1.wireOp",EDGE,"E46.0.3")]}),1.0]])],"derivedFrom":subQ1})])],"isStart":false}),makeQuery(id+"F4.opExtrude","SWEPT_FACE",FACE,{"disambiguationData":[OSD([subQ0])]})],"blendedInto":[makeQuery(id+"F4.opExtrude","SWEPT_FACE",FACE,{"disambiguationData":[OSD([subQ0])]})]});}
            var Q11;
            Q11=makeQuery(id+"F5.opFillet","BLEND_EDGE",EDGE,{"blendedFrom":[makeQuery(id+"F3.opExtrude","CAP_EDGE",EDGE,{"disambiguationData":[OSD([sQuery(id+"F1.wireOp",EDGE,"E46.0.2")])],"isStart":false}),makeQuery(id+"F3.opExtrude","SWEPT_FACE",FACE,{"disambiguationData":[OSD([sQuery(id+"F1.wireOp",EDGE,"E48.trimOffspring")])]})],"blendedInto":[makeQuery(id+"F3.opExtrude","SWEPT_FACE",FACE,{"disambiguationData":[OSD([sQuery(id+"F1.wireOp",EDGE,"E48.trimOffspring")])]})]});
            var Q12;
            Q12=makeQuery(id+"F5.opFillet","BLEND_EDGE",EDGE,{"blendedFrom":[makeQuery(id+"F3.opExtrude","CAP_EDGE",EDGE,{"disambiguationData":[OSD([sQuery(id+"F1.wireOp",EDGE,"E46.0.3")])],"isStart":false}),makeQuery(id+"F3.opExtrude","SWEPT_FACE",FACE,{"disambiguationData":[OSD([sQuery(id+"F1.wireOp",EDGE,"E48.trimOffspring")])]})],"blendedInto":[makeQuery(id+"F3.opExtrude","SWEPT_FACE",FACE,{"disambiguationData":[OSD([sQuery(id+"F1.wireOp",EDGE,"E48.trimOffspring")])]})]});
            var Q13;
            Q13=makeQuery(id+"F5.opFillet","BLEND_EDGE",EDGE,{"blendedFrom":[makeQuery(id+"F3.opExtrude","CAP_EDGE",EDGE,{"disambiguationData":[OSD([sQuery(id+"F1.wireOp",EDGE,"E46.0.3")])],"isStart":false}),makeQuery(id+"F3.opExtrude","SWEPT_FACE",FACE,{"disambiguationData":[OSD([sQuery(id+"F1.wireOp",EDGE,"E34.MirrorCS")])]})],"blendedInto":[makeQuery(id+"F3.opExtrude","SWEPT_FACE",FACE,{"disambiguationData":[OSD([sQuery(id+"F1.wireOp",EDGE,"E34.MirrorCS")])]})]});
            var Q14;
            Q14=makeQuery(id+"F3.opExtrude","CAP_EDGE",EDGE,{"disambiguationData":[OSD([sQuery(id+"F1.wireOp",EDGE,"E34.MirrorCS")])],"isStart":false});
            var Q15;
            Q15=makeQuery(id+"F3.opExtrude","SWEPT_EDGE",EDGE,{"disambiguationData":[OSD([sQuery(id+"F1.wireOp",EDGE,"E46.0.3"),sQuery(id+"F1.wireOp",EDGE,"E48.trimOffspring")])]});
            var Q16;
            Q16=makeQuery(id+"F3.opExtrude","SWEPT_EDGE",EDGE,{"disambiguationData":[OSD([sQuery(id+"F1.wireOp",EDGE,"E34.MirrorCS"),sQuery(id+"F1.wireOp",EDGE,"E46.0.3")])]});
            var Q17;
            {var subQ0=sQuery(id+"F1.wireOp",EDGE,"E34.MirrorCS");var subQ1=sQuery(id+"F1.wireOp",EDGE,"E46.0.2");Q17=makeQuery(id+"F5.opFillet","BLEND_EDGE",EDGE,{"blendedFrom":[makeQuery(id+"F4.opExtrude","CAP_EDGE",EDGE,{"disambiguationData":[OSD([subQ1]),TDD([makeQuery(id+"F1.imprint","IMPRINT",EDGE,{"disambiguationData":[TD([[makeQuery(id+"F1.imprint","INTERSECT",VERTEX,{"derivedFrom":[subQ0,subQ1]}),1.0]])],"derivedFrom":subQ1})])],"isStart":false}),makeQuery(id+"F4.opExtrude","SWEPT_FACE",FACE,{"disambiguationData":[OSD([subQ0])]})],"blendedInto":[makeQuery(id+"F4.opExtrude","SWEPT_FACE",FACE,{"disambiguationData":[OSD([subQ0])]})]});}
            var Q18;
            Q18=makeQuery(id+"F3.opExtrude","SWEPT_EDGE",EDGE,{"disambiguationData":[OSD([sQuery(id+"F1.wireOp",EDGE,"E34.MirrorCS"),sQuery(id+"F1.wireOp",EDGE,"E46.0.2")])]});
            var Q19;
            Q19=makeQuery(id+"F3.opExtrude","SWEPT_EDGE",EDGE,{"disambiguationData":[OSD([sQuery(id+"F1.wireOp",EDGE,"E46.0.2"),sQuery(id+"F1.wireOp",EDGE,"E48.trimOffspring")])]});
            fillet(context, id + "F7", {"entities" : qUnion([Q0, Q1, Q2, Q3, Q4, Q5, Q6, Q7, Q8, Q9, Q10, Q11, Q12, Q13, Q14, Q15, Q16, Q17, Q18, Q19]), "radius" : 0.13 * mm, "tangentPropagation" : true, "allowEdgeOverflow" : false});
        }
    });
